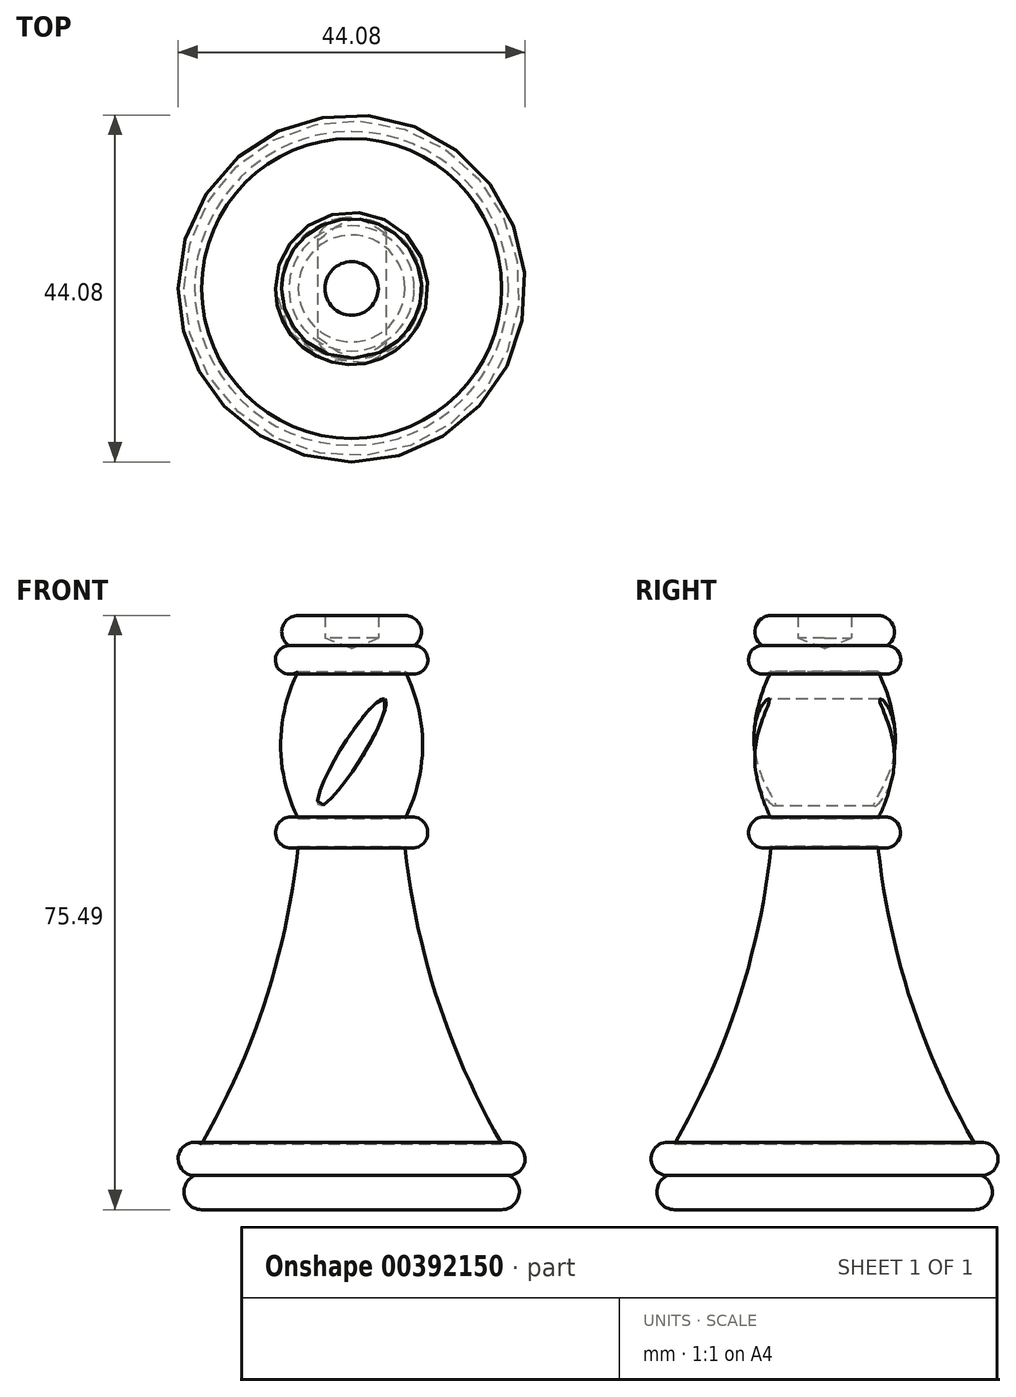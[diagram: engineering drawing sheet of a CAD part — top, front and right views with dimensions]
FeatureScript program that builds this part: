
annotation { "Feature Type Name" : "Feature", "Feature Type Description" : "" }
export const myFeature = defineFeature(function(context is Context, id is Id, definition is map)
    precondition{}
    {
        {
            var Q0;
            Q0=qCreatedBy(makeId("Front.planeOp"),FACE);
            var sketch = newSketch(context, id + "F0", { "sketchPlane" : qUnion([Q0])});
            skLineSegment(sketch, "E0", {"start": v(0, -29.68) * mm, "end": v(0, 33.82) * mm});
            skLineSegment(sketch, "E1", {"start": v(0, -29.68) * mm, "end": v(-19.05, -29.68) * mm});
            skArc(sketch, "E2", {"start": v(-19.05, -25.16) * mm, "mid": v(-21.3, -27.42) * mm, "end": v(-19.05, -29.68) * mm});
            skArc(sketch, "E3", {"start": v(-19.05, -21.3) * mm, "mid": v(-22.04, -23.23) * mm, "end": v(-19.05, -25.16) * mm});
            skArc(sketch, "E4", {"start": v(-19.05, -21.3) * mm, "mid": v(-10.94, -3.06) * mm, "end": v(-6.78, 16.45) * mm});
            skArc(sketch, "E5", {"start": v(-6.78, 20) * mm, "mid": v(-9.66, 18.23) * mm, "end": v(-6.78, 16.45) * mm});
            skArc(sketch, "E6", {"start": v(-6.78, 38.71) * mm, "mid": v(-9.02, 29.36) * mm, "end": v(-6.78, 20) * mm});
            skArc(sketch, "E7", {"start": v(-6.78, 41.62) * mm, "mid": v(-9.69, 40.17) * mm, "end": v(-6.78, 38.71) * mm});
            skLineSegment(sketch, "E8", {"start": v(0, 41.62) * mm, "end": v(0, 33.82) * mm});
            skArc(sketch, "E9", {"start": v(-6.78, 45.81) * mm, "mid": v(-8.87, 43.72) * mm, "end": v(-6.78, 41.62) * mm});
            skLineSegment(sketch, "E10", {"start": v(-6.78, 45.81) * mm, "end": v(-3.39, 45.81) * mm});
            skLineSegment(sketch, "E11", {"start": v(-3.39, 45.81) * mm, "end": v(-3.39, 42.9) * mm});
            skPoint(sketch, "E11.endSnap0", {"position": v(-3.39, 45.81) * mm});
            skLineSegment(sketch, "E12", {"start": v(-3.39, 42.9) * mm, "end": v(0, 41.62) * mm});
            skPoint(sketch, "E13.orphan", {"position": v(0, 45.81) * mm});
            skSolve(sketch);
        }
        {
            var Q0;
            Q0 = qSketchRegion(id + "F0", true);
            var Q1;
            Q1=sQuery(id+"F0.wireOp",EDGE,"E0");
            revolve(context, id + "F1", {"entities" : qUnion([Q0]), "axis" : qUnion([Q1]), "revolveType" : RevolveType.FULL});
        }
        {
            var Q0;
            Q0=qCreatedBy(makeId("Front.planeOp"),FACE);
            var sketch = newSketch(context, id + "F2", { "sketchPlane" : qUnion([Q0])});
            skEllipse(sketch, "E14", {"center": v(0, 28.4) * mm, "majorRadius": 7.97 * mm, "minorRadius": 1.4 * mm, "majorAxis": v(0.53, 0.85)});
            skSolve(sketch);
        }
        {
            var Q0;
            Q0 = qSketchRegion(id + "F2", true);
            extrude(context, id + "F3", {"entities" : qUnion([Q0]), "operationType" : NewBodyOperationType.REMOVE, "oppositeDirection" : true, "depth" : 25.4 * mm});
        }
        {
            var Q0;
            Q0 = qSketchRegion(id + "F2", true);
            extrude(context, id + "F4", {"entities" : qUnion([Q0]), "operationType" : NewBodyOperationType.REMOVE, "depth" : 77.72 * mm});
        }
    });
